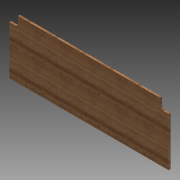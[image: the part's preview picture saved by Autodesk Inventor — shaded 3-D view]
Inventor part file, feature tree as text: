
AUTODESK INVENTOR PART (.ipt)
format: ipt  version: 2012 (Build 160160000, 160)  size: 102,912 bytes
history: native  units: in
note: dims shown in document units (in); Inventor stores cm internally (conversion verified against a paired STEP export)
features: extrude x1, sketch x1
ambient origin geometry x8: Origin, YZ Plane, XZ Plane, XY Plane, X Axis, Y Axis, Z Axis, Center Point
bodies: Solid1 (feature_tree)
feature tree (2):
  extrude  "Extrusion1"  Depth=20.5in
  sketch  "Sketch1"  dims[d0=7.5in d1=20.5in d2=0.25in d3=0.0in d4=1.0in d5=1.0in d6=0.625in d7=0.75in d8=0.625in d9=0.75in]
